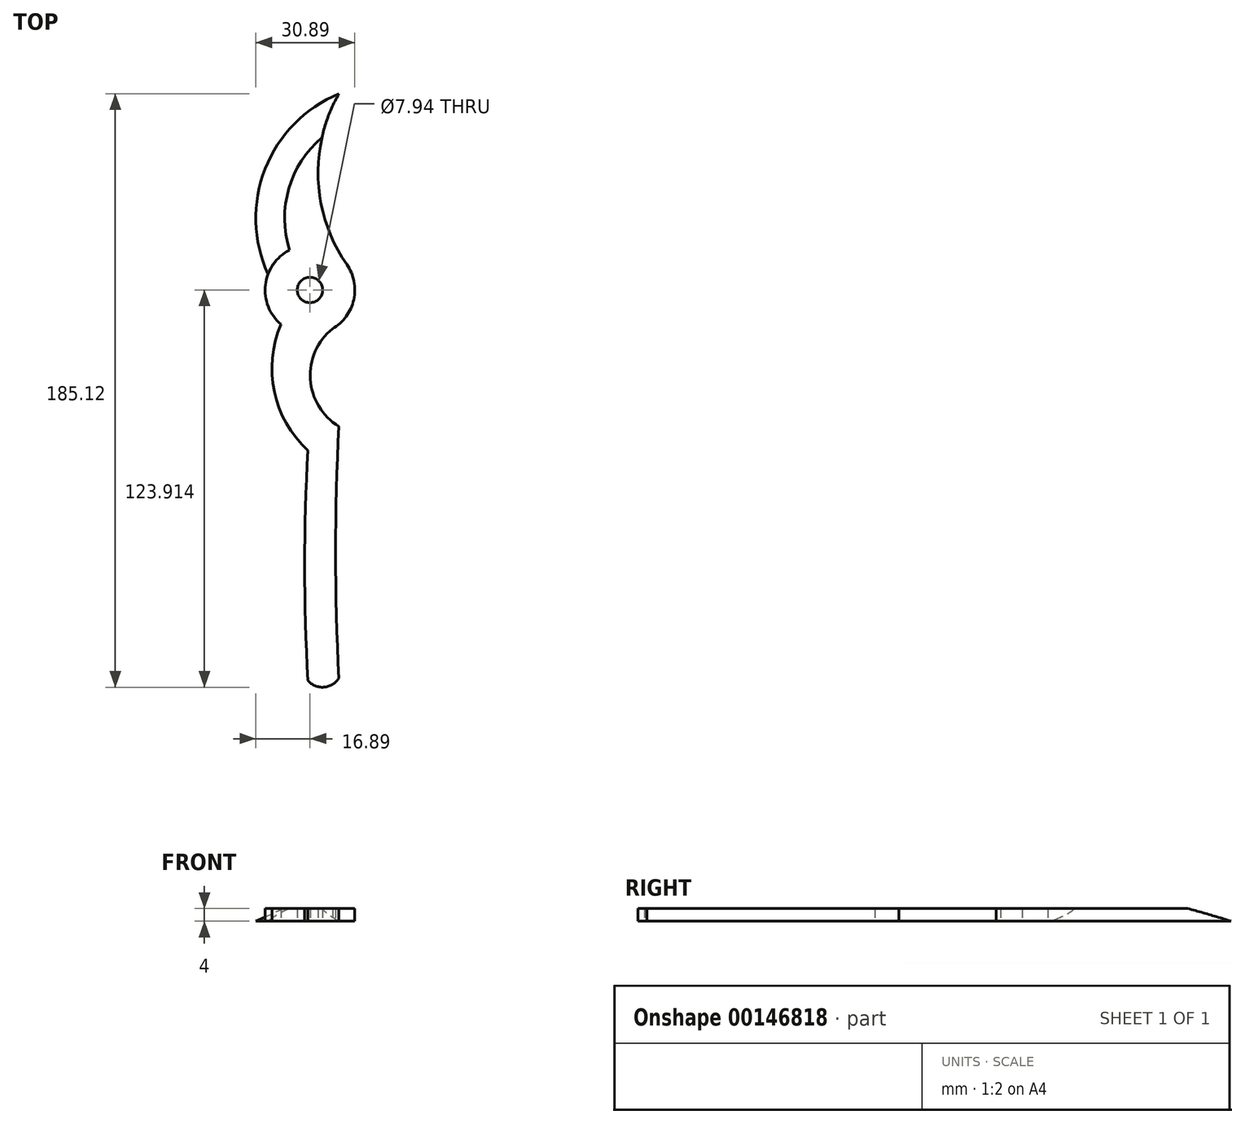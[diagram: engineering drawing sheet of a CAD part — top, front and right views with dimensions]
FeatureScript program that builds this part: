
annotation { "Feature Type Name" : "Feature", "Feature Type Description" : "" }
export const myFeature = defineFeature(function(context is Context, id is Id, definition is map)
    precondition{}
    {
        {
            var Q0;
            Q0=qCreatedBy(makeId("Top.planeOp"),FACE);
            var sketch = newSketch(context, id + "F0", { "sketchPlane" : qUnion([Q0])});
            skLineSegment(sketch, "E0", {"start": v(0, 0) * mm, "end": v(-18, 0) * mm});
            skCircle(sketch, "E1", {"center": v(-9, 10.72) * mm, "radius": 3.97 * mm});
            skCircle(sketch, "E2", {"center": v(-9, 10.72) * mm, "radius": 14 * mm});
            skArc(sketch, "E3.MirrorCS", {"start": v(0, -110.4) * mm, "mid": v(-4.63, -113.18) * mm, "end": v(-9.62, -111.1) * mm});
            skArc(sketch, "E4.MirrorCS", {"start": v(-9.62, -111.1) * mm, "mid": v(-10.63, -75.2) * mm, "end": v(-9.62, -39.3) * mm});
            skArc(sketch, "E5.MirrorCS", {"start": v(0, -110.4) * mm, "mid": v(-1, -71.1) * mm, "end": v(0, -31.8) * mm});
            skArc(sketch, "E6.MirrorCS", {"start": v(-9.62, -39.3) * mm, "mid": v(-20.34, -19.89) * mm, "end": v(-17.03, 2.04) * mm});
            skArc(sketch, "E7.MirrorCS", {"start": v(0, -31.8) * mm, "mid": v(-8.92, -15.9) * mm, "end": v(0, 0) * mm});
            skArc(sketch, "E8", {"start": v(0, 71.93) * mm, "mid": v(-6.43, 44.97) * mm, "end": v(2.49, 18.73) * mm});
            skArc(sketch, "E9", {"start": v(0, 71.93) * mm, "mid": v(-22.99, 48.5) * mm, "end": v(-22.1, 15.68) * mm});
            skArc(sketch, "E10", {"start": v(-4.86, 59.93) * mm, "mid": v(-15.28, 43.16) * mm, "end": v(-14.88, 23.43) * mm});
            skSolve(sketch);
        }
        {
            var Q0;
            Q0=qSketchRegion(id+"F0",true);
            extrude(context, id + "F1", {"entities" : qUnion([Q0]), "depth" : 4 * mm});
        }
        {
            var Q0;
            Q0=makeQuery(id+"F1.opExtrude","CAP_EDGE",EDGE,{"disambiguationData":[OSD([sQuery(id+"F0.wireOp",EDGE,"E9")])],"isStart":false});
            chamfer(context, id + "F2", {"entities" : qUnion([Q0]), "chamferType" : ChamferType.TWO_OFFSETS, "width1" : 9 * mm, "oppositeDirection" : false, "width2" : 4 * mm, "tangentPropagation" : true});
        }
    });
